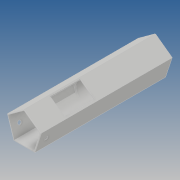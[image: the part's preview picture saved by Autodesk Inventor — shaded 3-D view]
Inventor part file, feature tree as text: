
AUTODESK INVENTOR PART (.ipt)
format: ipt  version: 2019 (Build 230136000, 136)  size: 241,664 bytes
history: native  units: mm
features: projected_geometry x10, sketch x9, extrude x6, chamfer x4, hole x2, other x2, fillet x2, mirror x1
ambient origin geometry x8: Origin, YZ Plane, XZ Plane, XY Plane, X Axis, Y Axis, Z Axis, Center Point
bodies: Body1 (feature_tree)
feature tree (36):
  extrude  "Extrusion2"  Depth=16.0mm
  hole  "Perçage1"  [1 undecoded]
  mirror  "Symétrie1"
  other  "Plan de construction1"
  extrude  "Extrusion3"  Depth=150.0mm TaperAngle=0.0deg
  extrude  "Extrusion4"  Depth=10.0mm
  chamfer  "Chanfrein1"  [1 undecoded]
  extrude  "Extrusion5"  Depth=30.0mm
  other  "Hélicoïde1"
  fillet  "Congé1"  Radius=100.0mm
  fillet  "Congé2"  Radius=5.0mm
  extrude  "Extrusion8"  Depth=1.0mm TaperAngle=45.0deg
  extrude  "Extrusion10"  Depth=6.5mm
  chamfer  "Chanfrein3"  Distance=1.0mm
  chamfer  "Chanfrein4"  Distance=37.0mm
  chamfer  "Chanfrein5"  Distance=10.0mm
  hole  "Perçage2"  [1 undecoded]
  sketch  "Esquisse2"
  sketch  "Esquisse3"
  projected_geometry  "Boucle projetée1"
  sketch  "Esquisse4"
  projected_geometry  "Boucle projetée2"
  sketch  "Esquisse5"
  projected_geometry  "Boucle projetée3"
  sketch  "Esquisse6"
  projected_geometry  "Boucle projetée4"
  sketch  "Esquisse8"
  projected_geometry  "Boucle projetée7"
  sketch  "Esquisse12"
  projected_geometry  "Boucle projetée13"
  sketch  "Esquisse14"
  projected_geometry  "Boucle projetée18"
  projected_geometry  "Boucle projetée19"
  projected_geometry  "Boucle projetée20"
  projected_geometry  "Boucle projetée21"
  sketch  "Esquisse17"
note: 3 required parameter values undecoded (feature->parameter linkage not recoverable at this tier; creation-order binding heuristic only, values carry confidence <= 0.55)
